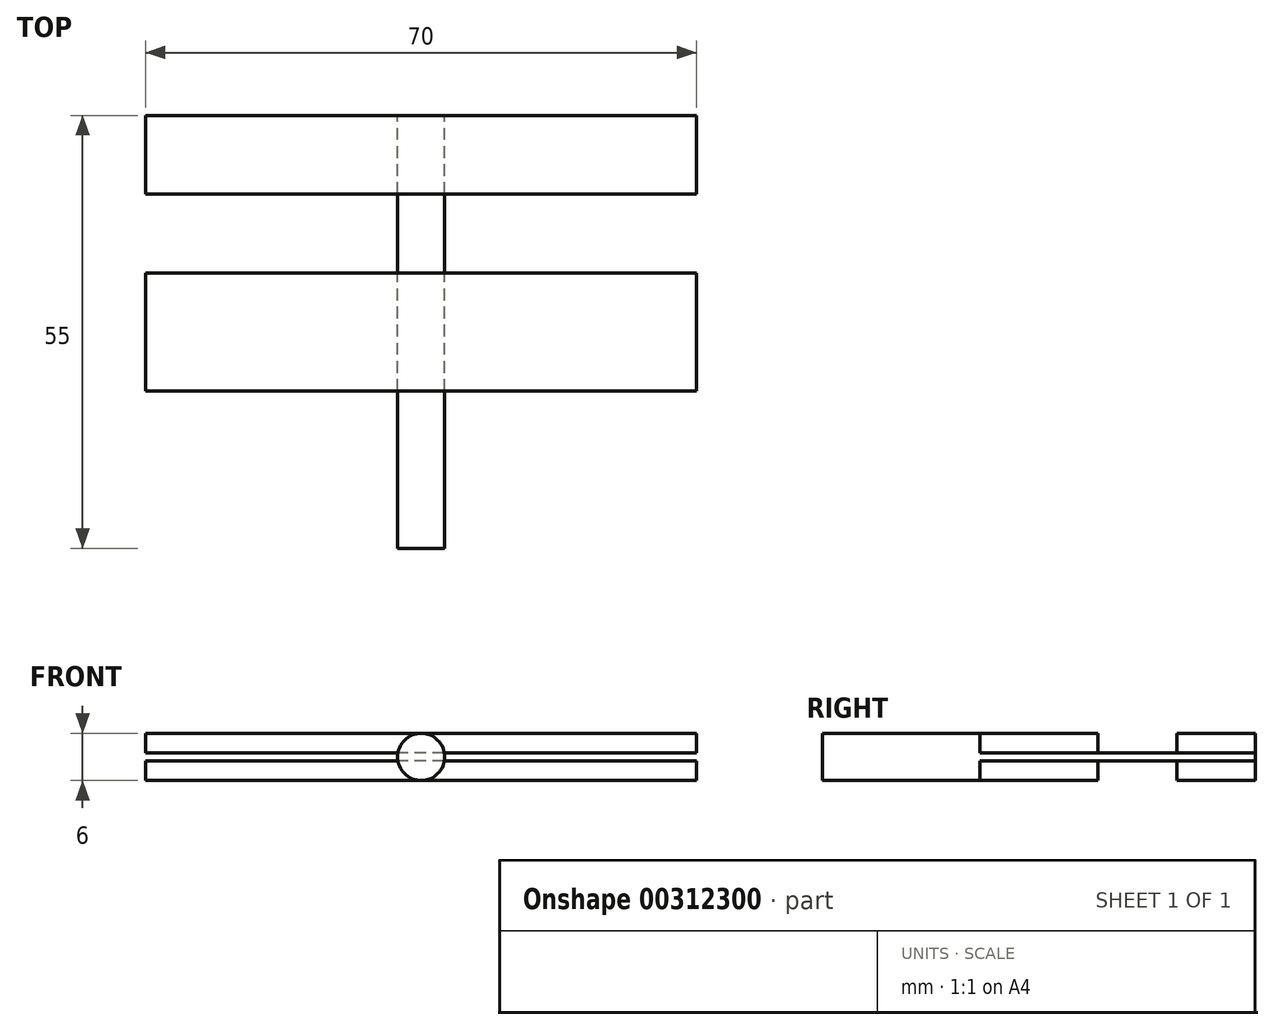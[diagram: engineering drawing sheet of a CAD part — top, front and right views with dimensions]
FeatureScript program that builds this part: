
annotation { "Feature Type Name" : "Feature", "Feature Type Description" : "" }
export const myFeature = defineFeature(function(context is Context, id is Id, definition is map)
    precondition{}
    {
        {
            var Q0;
            Q0=qCreatedBy(makeId("Front.planeOp"),FACE);
            var sketch = newSketch(context, id + "F0", { "sketchPlane" : qUnion([Q0])});
            skLineSegment(sketch, "E0.bottom", {"start": v(-35, 3) * mm, "end": v(35, 3) * mm});
            skLineSegment(sketch, "E0.top", {"start": v(-35, -3) * mm, "end": v(35, -3) * mm});
            skLineSegment(sketch, "E0.left", {"start": v(-35, 3) * mm, "end": v(-35, -3) * mm});
            skLineSegment(sketch, "E0.right", {"start": v(35, 3) * mm, "end": v(35, -3) * mm});
            skPoint(sketch, "E0.middle", {"position": v(0, 0) * mm});
            skCircle(sketch, "E1", {"center": v(0, 0) * mm, "radius": 3 * mm});
            skLineSegment(sketch, "E2.bottom", {"start": v(35, 0.5) * mm, "end": v(-35, 0.5) * mm});
            skLineSegment(sketch, "E2.top", {"start": v(35, -0.5) * mm, "end": v(-35, -0.5) * mm});
            skLineSegment(sketch, "E2.left", {"start": v(35, 0.5) * mm, "end": v(35, -0.5) * mm});
            skLineSegment(sketch, "E2.right", {"start": v(-35, 0.5) * mm, "end": v(-35, -0.5) * mm});
            skSolve(sketch);
        }
        {
            var Q0;
            {var subQ0=sQuery(id+"F0.wireOp",EDGE,"E0.left");var subQ1=sQuery(id+"F0.wireOp",EDGE,"E0.bottom");var subQ2=makeQuery(id+"F0.imprint","INTERSECT",VERTEX,{"derivedFrom":[subQ1,subQ0]});Q0=makeQuery(id+"F0.imprint","IMPRINT",FACE,{"disambiguationData":[TD([[makeQuery(id+"F0.imprint","IMPRINT",EDGE,{"disambiguationData":[TD([[subQ2,-1.0]])],"derivedFrom":subQ1}),-1.0]])]});}
            var Q1;
            {var subQ5=sQuery(id+"F0.wireOp",EDGE,"E2.right");Q1=makeQuery(id+"F0.imprint","IMPRINT",FACE,{"disambiguationData":[TD([[makeQuery(id+"F0.imprint","IMPRINT",EDGE,{"derivedFrom":subQ5}),1.0]])]});}
            var Q2;
            {var subQ0=sQuery(id+"F0.wireOp",EDGE,"E0.left");var subQ1=sQuery(id+"F0.wireOp",EDGE,"E0.top");var subQ2=makeQuery(id+"F0.imprint","INTERSECT",VERTEX,{"derivedFrom":[subQ1,subQ0]});Q2=makeQuery(id+"F0.imprint","IMPRINT",FACE,{"disambiguationData":[TD([[makeQuery(id+"F0.imprint","IMPRINT",EDGE,{"disambiguationData":[TD([[subQ2,-1.0]])],"derivedFrom":subQ1}),1.0]])]});}
            var Q3;
            {var subQ0=sQuery(id+"F0.wireOp",EDGE,"E1");var subQ1=makeQuery(id+"F0.imprint","INTERSECT",VERTEX,{"derivedFrom":[sQuery(id+"F0.wireOp",EDGE,"E0.top"),subQ0]});Q3=makeQuery(id+"F0.imprint","IMPRINT",FACE,{"disambiguationData":[TD([[makeQuery(id+"F0.imprint","IMPRINT",EDGE,{"disambiguationData":[TD([[subQ1,1.0]])],"derivedFrom":subQ0}),1.0]])]});}
            var Q4;
            {var subQ0=sQuery(id+"F0.wireOp",EDGE,"E1");var subQ1=makeQuery(id+"F0.imprint","INTERSECT",VERTEX,{"derivedFrom":[sQuery(id+"F0.wireOp",EDGE,"E0.bottom"),subQ0]});Q4=makeQuery(id+"F0.imprint","IMPRINT",FACE,{"disambiguationData":[TD([[makeQuery(id+"F0.imprint","IMPRINT",EDGE,{"disambiguationData":[TD([[subQ1,1.0]])],"derivedFrom":subQ0}),1.0]])]});}
            var Q5;
            {var subQ0=sQuery(id+"F0.wireOp",EDGE,"E0.right");var subQ1=sQuery(id+"F0.wireOp",EDGE,"E0.bottom");var subQ2=makeQuery(id+"F0.imprint","INTERSECT",VERTEX,{"derivedFrom":[subQ1,subQ0]});Q5=makeQuery(id+"F0.imprint","IMPRINT",FACE,{"disambiguationData":[TD([[makeQuery(id+"F0.imprint","IMPRINT",EDGE,{"disambiguationData":[TD([[subQ2,1.0]])],"derivedFrom":subQ1}),-1.0]])]});}
            var Q6;
            {var subQ5=sQuery(id+"F0.wireOp",EDGE,"E2.left");Q6=makeQuery(id+"F0.imprint","IMPRINT",FACE,{"disambiguationData":[TD([[makeQuery(id+"F0.imprint","IMPRINT",EDGE,{"derivedFrom":subQ5}),-1.0]])]});}
            var Q7;
            {var subQ0=sQuery(id+"F0.wireOp",EDGE,"E0.right");var subQ1=sQuery(id+"F0.wireOp",EDGE,"E0.top");var subQ2=makeQuery(id+"F0.imprint","INTERSECT",VERTEX,{"derivedFrom":[subQ1,subQ0]});Q7=makeQuery(id+"F0.imprint","IMPRINT",FACE,{"disambiguationData":[TD([[makeQuery(id+"F0.imprint","IMPRINT",EDGE,{"disambiguationData":[TD([[subQ2,1.0]])],"derivedFrom":subQ1}),1.0]])]});}
            var Q8;
            {var subQ0=sQuery(id+"F0.wireOp",EDGE,"E2.bottom");var subQ1=sQuery(id+"F0.wireOp",EDGE,"E1");var subQ2=makeQuery(id+"F0.imprint","INTERSECT",VERTEX,{"disambiguationData":[OD(1.0)],"derivedFrom":[subQ1,subQ0]});Q8=makeQuery(id+"F0.imprint","IMPRINT",FACE,{"disambiguationData":[TD([[makeQuery(id+"F0.imprint","IMPRINT",EDGE,{"disambiguationData":[TD([[subQ2,-1.0]])],"derivedFrom":subQ1}),1.0]])]});}
            extrude(context, id + "F1", {"entities" : qUnion([Q0, Q1, Q2, Q3, Q4, Q5, Q6, Q7, Q8]), "depth" : 10 * mm});
        }
        {
            var Q0;
            {var subQ5=sQuery(id+"F0.wireOp",EDGE,"E2.right");Q0=makeQuery(id+"F0.imprint","IMPRINT",FACE,{"disambiguationData":[TD([[makeQuery(id+"F0.imprint","IMPRINT",EDGE,{"derivedFrom":subQ5}),1.0]])]});}
            var Q1;
            {var subQ0=sQuery(id+"F0.wireOp",EDGE,"E2.bottom");var subQ1=sQuery(id+"F0.wireOp",EDGE,"E1");var subQ2=makeQuery(id+"F0.imprint","INTERSECT",VERTEX,{"disambiguationData":[OD(1.0)],"derivedFrom":[subQ1,subQ0]});Q1=makeQuery(id+"F0.imprint","IMPRINT",FACE,{"disambiguationData":[TD([[makeQuery(id+"F0.imprint","IMPRINT",EDGE,{"disambiguationData":[TD([[subQ2,-1.0]])],"derivedFrom":subQ1}),1.0]])]});}
            var Q2;
            {var subQ5=sQuery(id+"F0.wireOp",EDGE,"E2.left");Q2=makeQuery(id+"F0.imprint","IMPRINT",FACE,{"disambiguationData":[TD([[makeQuery(id+"F0.imprint","IMPRINT",EDGE,{"derivedFrom":subQ5}),-1.0]])]});}
            extrude(context, id + "F2", {"entities" : qUnion([Q0, Q1, Q2]), "operationType" : NewBodyOperationType.ADD, "depth" : 20 * mm, "hasSecondDirection" : true, "secondDirectionOppositeDirection" : false, "secondDirectionDepth" : 10 * mm});
        }
        {
            var Q0;
            {var subQ0=sQuery(id+"F0.wireOp",EDGE,"E0.right");var subQ1=sQuery(id+"F0.wireOp",EDGE,"E0.bottom");var subQ2=makeQuery(id+"F0.imprint","INTERSECT",VERTEX,{"derivedFrom":[subQ1,subQ0]});Q0=makeQuery(id+"F0.imprint","IMPRINT",FACE,{"disambiguationData":[TD([[makeQuery(id+"F0.imprint","IMPRINT",EDGE,{"disambiguationData":[TD([[subQ2,1.0]])],"derivedFrom":subQ1}),-1.0]])]});}
            var Q1;
            {var subQ5=sQuery(id+"F0.wireOp",EDGE,"E2.left");Q1=makeQuery(id+"F0.imprint","IMPRINT",FACE,{"disambiguationData":[TD([[makeQuery(id+"F0.imprint","IMPRINT",EDGE,{"derivedFrom":subQ5}),-1.0]])]});}
            var Q2;
            {var subQ0=sQuery(id+"F0.wireOp",EDGE,"E0.right");var subQ1=sQuery(id+"F0.wireOp",EDGE,"E0.top");var subQ2=makeQuery(id+"F0.imprint","INTERSECT",VERTEX,{"derivedFrom":[subQ1,subQ0]});Q2=makeQuery(id+"F0.imprint","IMPRINT",FACE,{"disambiguationData":[TD([[makeQuery(id+"F0.imprint","IMPRINT",EDGE,{"disambiguationData":[TD([[subQ2,1.0]])],"derivedFrom":subQ1}),1.0]])]});}
            var Q3;
            {var subQ0=sQuery(id+"F0.wireOp",EDGE,"E0.left");var subQ1=sQuery(id+"F0.wireOp",EDGE,"E0.top");var subQ2=makeQuery(id+"F0.imprint","INTERSECT",VERTEX,{"derivedFrom":[subQ1,subQ0]});Q3=makeQuery(id+"F0.imprint","IMPRINT",FACE,{"disambiguationData":[TD([[makeQuery(id+"F0.imprint","IMPRINT",EDGE,{"disambiguationData":[TD([[subQ2,-1.0]])],"derivedFrom":subQ1}),1.0]])]});}
            var Q4;
            {var subQ0=sQuery(id+"F0.wireOp",EDGE,"E0.left");var subQ1=sQuery(id+"F0.wireOp",EDGE,"E0.bottom");var subQ2=makeQuery(id+"F0.imprint","INTERSECT",VERTEX,{"derivedFrom":[subQ1,subQ0]});Q4=makeQuery(id+"F0.imprint","IMPRINT",FACE,{"disambiguationData":[TD([[makeQuery(id+"F0.imprint","IMPRINT",EDGE,{"disambiguationData":[TD([[subQ2,-1.0]])],"derivedFrom":subQ1}),-1.0]])]});}
            var Q5;
            {var subQ5=sQuery(id+"F0.wireOp",EDGE,"E2.right");Q5=makeQuery(id+"F0.imprint","IMPRINT",FACE,{"disambiguationData":[TD([[makeQuery(id+"F0.imprint","IMPRINT",EDGE,{"derivedFrom":subQ5}),1.0]])]});}
            var Q6;
            {var subQ0=sQuery(id+"F0.wireOp",EDGE,"E1");var subQ1=makeQuery(id+"F0.imprint","INTERSECT",VERTEX,{"derivedFrom":[sQuery(id+"F0.wireOp",EDGE,"E0.bottom"),subQ0]});Q6=makeQuery(id+"F0.imprint","IMPRINT",FACE,{"disambiguationData":[TD([[makeQuery(id+"F0.imprint","IMPRINT",EDGE,{"disambiguationData":[TD([[subQ1,1.0]])],"derivedFrom":subQ0}),1.0]])]});}
            var Q7;
            {var subQ0=sQuery(id+"F0.wireOp",EDGE,"E2.bottom");var subQ1=sQuery(id+"F0.wireOp",EDGE,"E1");var subQ2=makeQuery(id+"F0.imprint","INTERSECT",VERTEX,{"disambiguationData":[OD(1.0)],"derivedFrom":[subQ1,subQ0]});Q7=makeQuery(id+"F0.imprint","IMPRINT",FACE,{"disambiguationData":[TD([[makeQuery(id+"F0.imprint","IMPRINT",EDGE,{"disambiguationData":[TD([[subQ2,-1.0]])],"derivedFrom":subQ1}),1.0]])]});}
            var Q8;
            {var subQ0=sQuery(id+"F0.wireOp",EDGE,"E1");var subQ1=makeQuery(id+"F0.imprint","INTERSECT",VERTEX,{"derivedFrom":[sQuery(id+"F0.wireOp",EDGE,"E0.top"),subQ0]});Q8=makeQuery(id+"F0.imprint","IMPRINT",FACE,{"disambiguationData":[TD([[makeQuery(id+"F0.imprint","IMPRINT",EDGE,{"disambiguationData":[TD([[subQ1,1.0]])],"derivedFrom":subQ0}),1.0]])]});}
            extrude(context, id + "F3", {"entities" : qUnion([Q0, Q1, Q2, Q3, Q4, Q5, Q6, Q7, Q8]), "operationType" : NewBodyOperationType.ADD, "depth" : 35 * mm, "hasSecondDirection" : true, "secondDirectionOppositeDirection" : false, "secondDirectionDepth" : 20 * mm});
        }
        {
            var Q0;
            {var subQ0=sQuery(id+"F0.wireOp",EDGE,"E1");var subQ1=makeQuery(id+"F0.imprint","INTERSECT",VERTEX,{"derivedFrom":[sQuery(id+"F0.wireOp",EDGE,"E0.top"),subQ0]});Q0=makeQuery(id+"F0.imprint","IMPRINT",FACE,{"disambiguationData":[TD([[makeQuery(id+"F0.imprint","IMPRINT",EDGE,{"disambiguationData":[TD([[subQ1,1.0]])],"derivedFrom":subQ0}),1.0]])]});}
            var Q1;
            {var subQ0=sQuery(id+"F0.wireOp",EDGE,"E2.bottom");var subQ1=sQuery(id+"F0.wireOp",EDGE,"E1");var subQ2=makeQuery(id+"F0.imprint","INTERSECT",VERTEX,{"disambiguationData":[OD(1.0)],"derivedFrom":[subQ1,subQ0]});Q1=makeQuery(id+"F0.imprint","IMPRINT",FACE,{"disambiguationData":[TD([[makeQuery(id+"F0.imprint","IMPRINT",EDGE,{"disambiguationData":[TD([[subQ2,-1.0]])],"derivedFrom":subQ1}),1.0]])]});}
            var Q2;
            {var subQ0=sQuery(id+"F0.wireOp",EDGE,"E1");var subQ1=makeQuery(id+"F0.imprint","INTERSECT",VERTEX,{"derivedFrom":[sQuery(id+"F0.wireOp",EDGE,"E0.bottom"),subQ0]});Q2=makeQuery(id+"F0.imprint","IMPRINT",FACE,{"disambiguationData":[TD([[makeQuery(id+"F0.imprint","IMPRINT",EDGE,{"disambiguationData":[TD([[subQ1,1.0]])],"derivedFrom":subQ0}),1.0]])]});}
            extrude(context, id + "F4", {"entities" : qUnion([Q0, Q1, Q2]), "operationType" : NewBodyOperationType.ADD, "depth" : 55 * mm, "hasSecondDirection" : true, "secondDirectionOppositeDirection" : false, "secondDirectionDepth" : 35 * mm});
        }
    });
